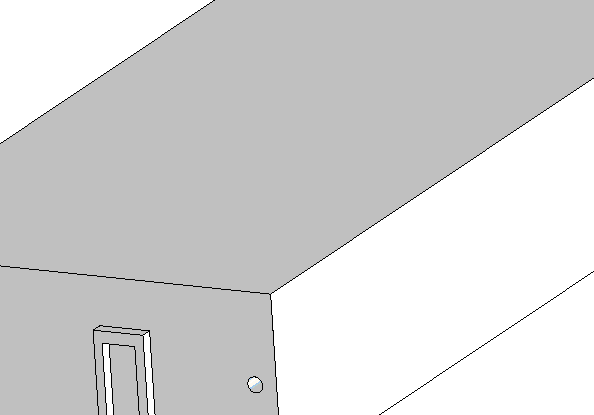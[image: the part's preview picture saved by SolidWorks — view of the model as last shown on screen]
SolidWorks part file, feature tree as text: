
SOLIDWORKS PART (.sldprt)
format: sldprt  version: not decoded by parser v0  size: 181,760 bytes
history: native  units: mm
features: sketch x6, extrude x3, cut_extrude x3, material x1 (+13 scaffold rows collapsed)
feature tree (26):
  scaffold x13  (default folders/planes/origin — collapsed)
  material  "Material <not specified>"
  sketch  "Sketch1"  dims[D1=40.5mm D2=100.0mm]
  extrude  "Extrude1"  Depth=200mm
  sketch  "Sketch2"  dims[D1=3.556mm D2=3.556mm D3=20.3mm D4=20.3mm D5=90.0mm D6=5.0mm]
  cut_extrude  "Cut-Extrude1"  Depth=10mm
  sketch  "Sketch3"  dims[D1=5.0mm D2=1.0mm]
  extrude  "Extrude2"  Depth=15mm
  sketch  "Sketch4"  dims[D1=3.556mm D2=3.556mm D3=70.0mm D4=211.0mm D5=15.0mm]
  cut_extrude  "Cut-Extrude2"  Depth=15mm
  sketch  "Sketch5"
  extrude  "Extrude3"  Depth=3mm
  sketch  "Sketch6"
  cut_extrude  "Cut-Extrude3"  Depth=3mm
decode coverage: 10 of 12 modeling features carry decoded parameters
note: suppression state not decoded; provenance and decode notes live in map.json
